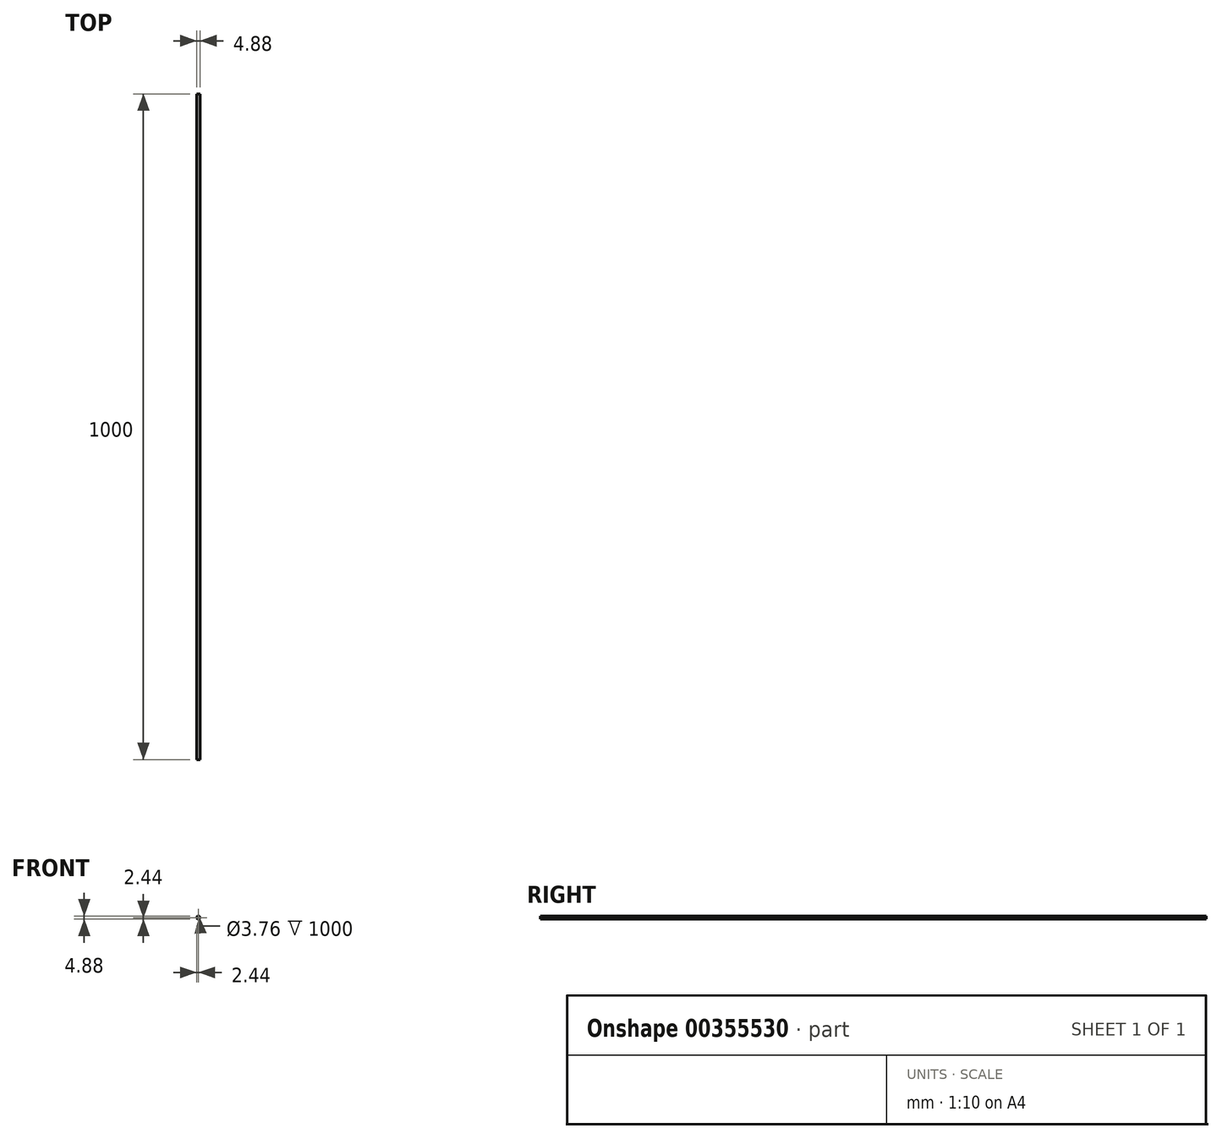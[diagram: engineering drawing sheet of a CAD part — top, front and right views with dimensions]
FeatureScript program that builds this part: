
annotation { "Feature Type Name" : "Feature", "Feature Type Description" : "" }
export const myFeature = defineFeature(function(context is Context, id is Id, definition is map)
    precondition{}
    {
        {
            var Q0;
            Q0=qCreatedBy(makeId("Front.planeOp"),FACE);
            var sketch = newSketch(context, id + "F0", { "sketchPlane" : qUnion([Q0])});
            skCircle(sketch, "E0", {"center": v(0, 0) * mm, "radius": 2.44 * mm});
            skCircle(sketch, "E1", {"center": v(0, 0) * mm, "radius": 1.88 * mm});
            skSolve(sketch);
        }
        {
            var Q0;
            Q0 = qSketchRegion(id + "F0", true);
            extrude(context, id + "F1", {"entities" : qUnion([Q0]), "depth" : 1000 * mm});
        }
    });
